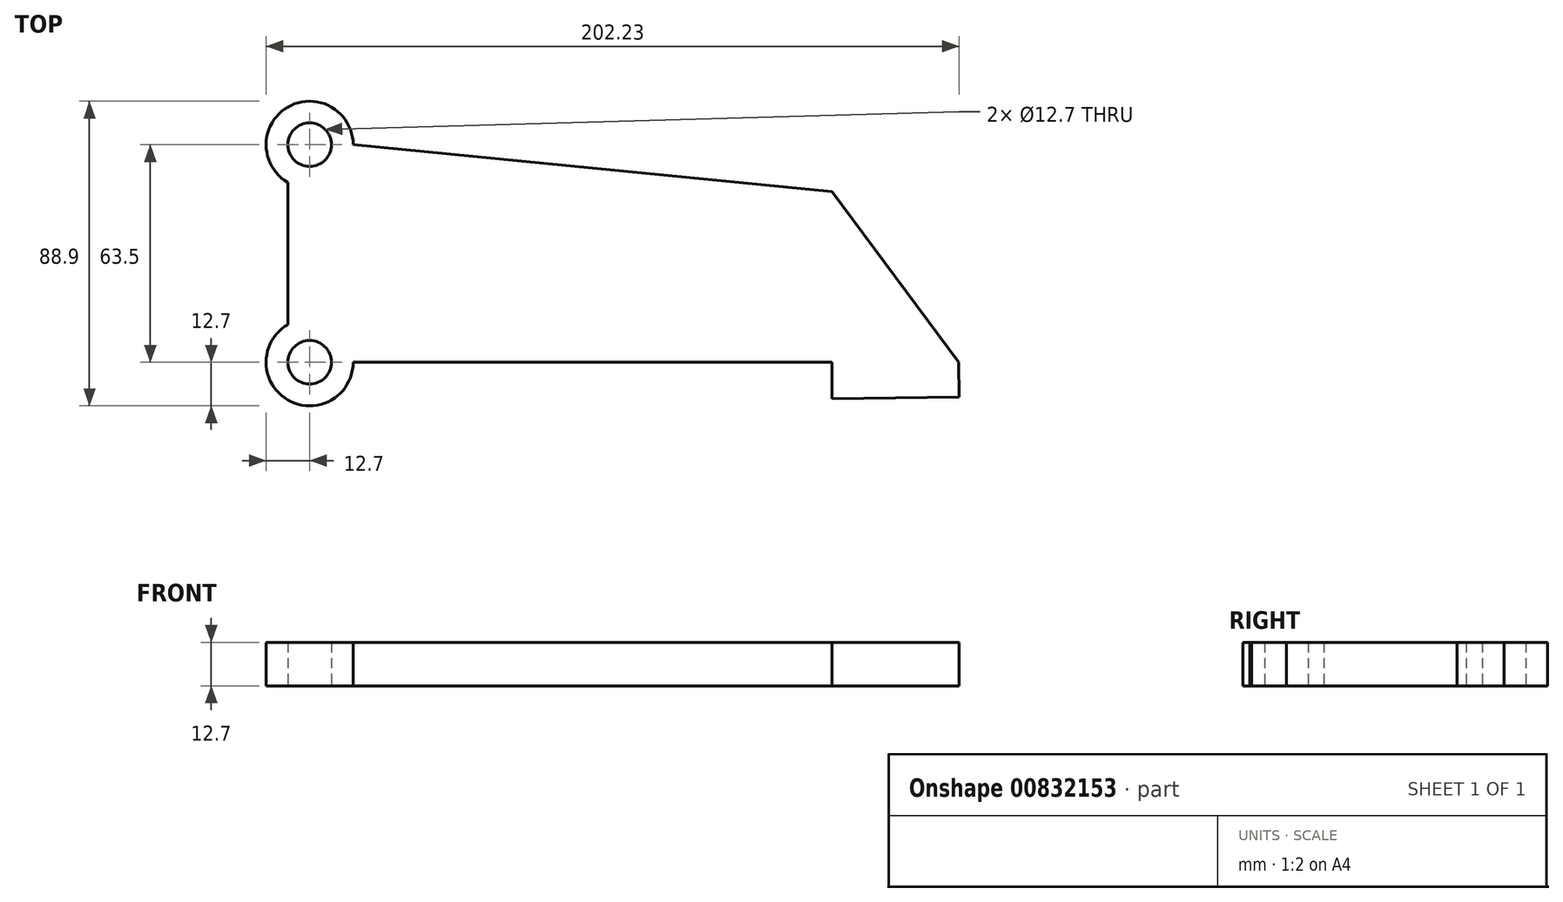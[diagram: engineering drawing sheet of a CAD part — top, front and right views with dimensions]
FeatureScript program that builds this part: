
annotation { "Feature Type Name" : "Feature", "Feature Type Description" : "" }
export const myFeature = defineFeature(function(context is Context, id is Id, definition is map)
    precondition{}
    {
        {
            var Q0;
            Q0=qCreatedBy(makeId("Top.planeOp"),FACE);
            var sketch = newSketch(context, id + "F0", { "sketchPlane" : qUnion([Q0])});
            skCircle(sketch, "E0", {"center": v(0, 0) * mm, "radius": 12.7 * mm});
            skLineSegment(sketch, "E1", {"start": v(0, 0) * mm, "end": v(0, 63.5) * mm});
            skCircle(sketch, "E2", {"center": v(0, 63.5) * mm, "radius": 12.7 * mm});
            skLineSegment(sketch, "E3", {"start": v(0, 0) * mm, "end": v(-12.7, 0) * mm});
            skLineSegment(sketch, "E4", {"start": v(-12.7, 0) * mm, "end": v(-6.35, 0) * mm});
            skLineSegment(sketch, "E5", {"start": v(-6.35, 0) * mm, "end": v(-6.35, 52.5) * mm});
            skCircle(sketch, "E6", {"center": v(0, 63.5) * mm, "radius": 6.35 * mm});
            skCircle(sketch, "E7", {"center": v(0, 0) * mm, "radius": 6.35 * mm});
            skLineSegment(sketch, "E8", {"start": v(0, 0) * mm, "end": v(152.4, 0) * mm});
            skLineSegment(sketch, "E9", {"start": v(152.4, 0) * mm, "end": v(152.4, -10.6) * mm});
            skLineSegment(sketch, "E10", {"start": v(152.4, -10.6) * mm, "end": v(189.53, -10.08) * mm});
            skLineSegment(sketch, "E11", {"start": v(189.53, -10.08) * mm, "end": v(189.39, 0) * mm});
            skLineSegment(sketch, "E12", {"start": v(189.39, 0) * mm, "end": v(152.4, 49.87) * mm});
            skLineSegment(sketch, "E13", {"start": v(152.4, 49.87) * mm, "end": v(12.7, 63.5) * mm});
            skSolve(sketch);
        }
        {
            var Q0;
            Q0 = qSketchRegion(id + "F0", true);
            extrude(context, id + "F1", {"entities" : qUnion([Q0]), "endBound" : BoundingType.SYMMETRIC, "depth" : 12.7 * mm, "offsetDistance" : 25.4 * mm});
        }
    });
